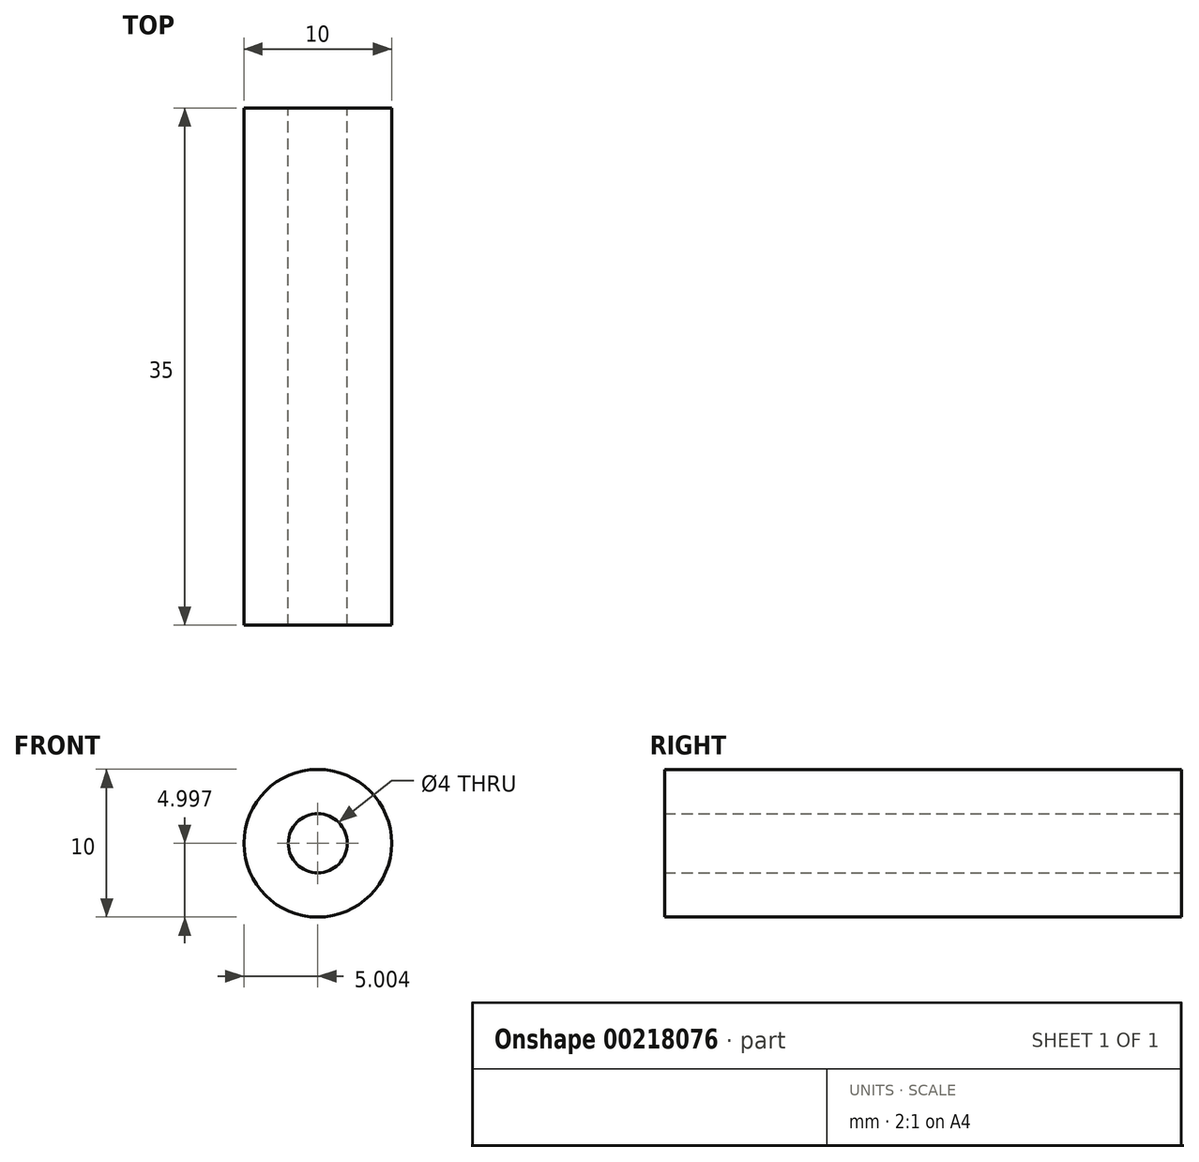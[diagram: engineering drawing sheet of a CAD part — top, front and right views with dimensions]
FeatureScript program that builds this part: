
annotation { "Feature Type Name" : "Feature", "Feature Type Description" : "" }
export const myFeature = defineFeature(function(context is Context, id is Id, definition is map)
    precondition{}
    {
        {
            var Q0;
            Q0=qCreatedBy(makeId("Front.planeOp"),FACE);
            var sketch = newSketch(context, id + "F0", { "sketchPlane" : qUnion([Q0])});
            skCircle(sketch, "E0", {"center": v(-21.55, 24.77) * mm, "radius": 5 * mm});
            skCircle(sketch, "E1", {"center": v(-21.55, 24.77) * mm, "radius": 2 * mm});
            skSolve(sketch);
        }
        {
            var Q0;
            Q0=makeQuery(id+"F0.imprint","IMPRINT",FACE,{"disambiguationData":[TD([[makeQuery(id+"F0.imprint","IMPRINT",EDGE,{"derivedFrom":sQuery(id+"F0.wireOp",EDGE,"E0")}),1.0]])]});
            extrude(context, id + "F1", {"entities" : qUnion([Q0]), "depth" : 35 * mm});
        }
    });
